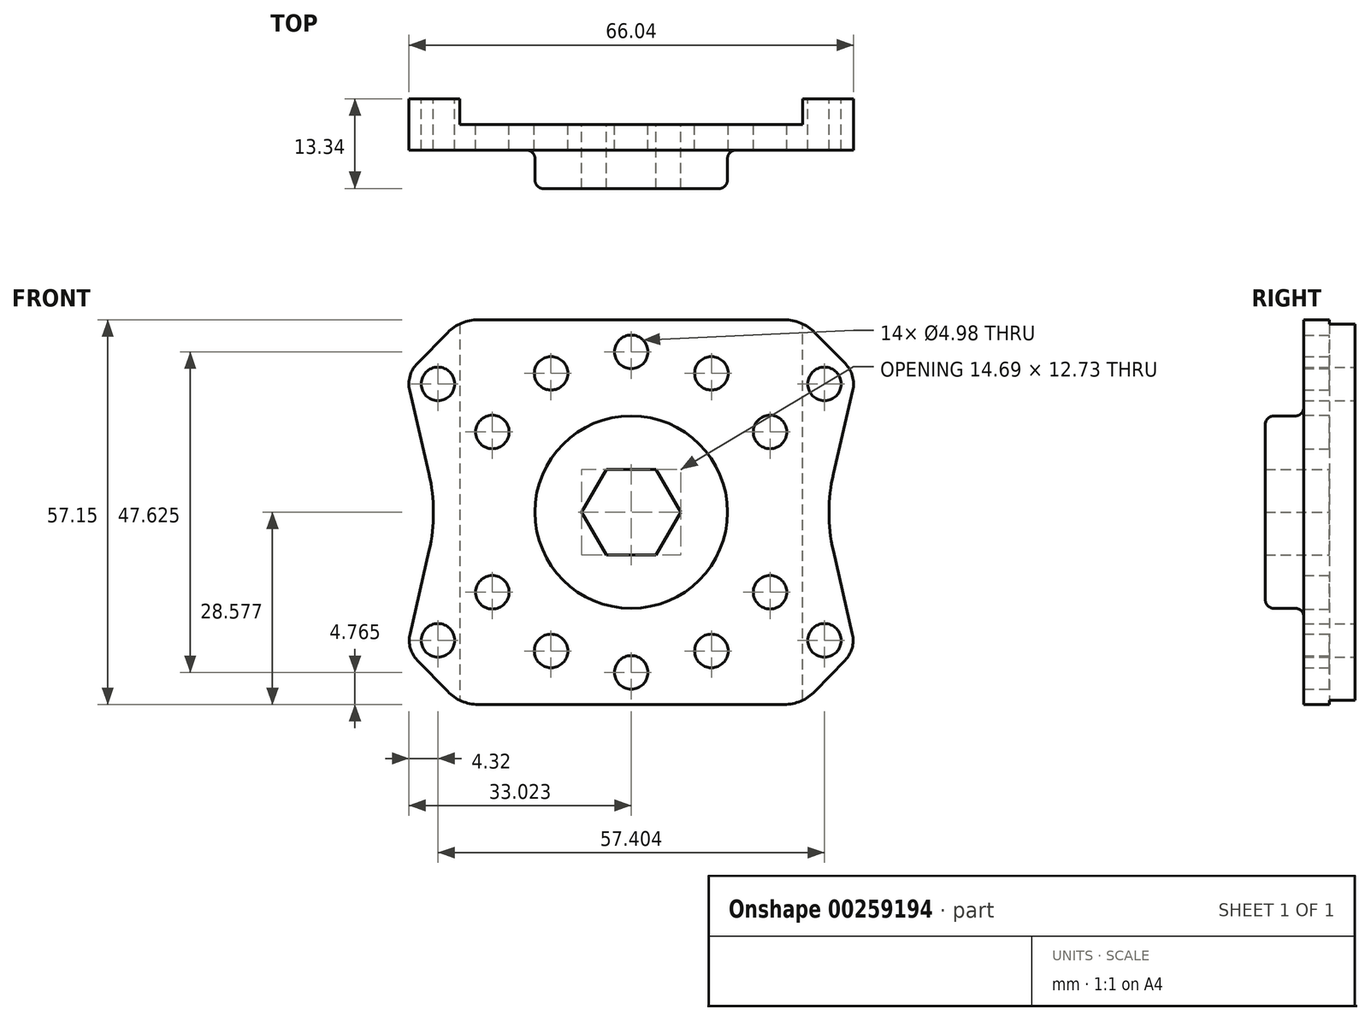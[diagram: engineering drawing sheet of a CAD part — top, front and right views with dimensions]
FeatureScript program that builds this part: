
annotation { "Feature Type Name" : "Feature", "Feature Type Description" : "" }
export const myFeature = defineFeature(function(context is Context, id is Id, definition is map)
    precondition{}
    {
        {
            var Q0;
            Q0=qCreatedBy(makeId("Front.planeOp"),FACE);
            var sketch = newSketch(context, id + "F0", { "sketchPlane" : qUnion([Q0])});
            skLineSegment(sketch, "E0.bottom", {"start": v(-23.4, 28.57) * mm, "end": v(22.07, 28.57) * mm});
            skLineSegment(sketch, "E0.top", {"start": v(-23.38, -28.58) * mm, "end": v(22.04, -28.58) * mm});
            skCircle(sketch, "E1", {"center": v(28.03, 19.05) * mm, "radius": 2.49 * mm});
            skCircle(sketch, "E2", {"center": v(28.03, -19.05) * mm, "radius": 2.49 * mm});
            skArc(sketch, "E3", {"start": v(32.24, 18.07) * mm, "mid": v(32.2, 20.21) * mm, "end": v(31.12, 22.07) * mm});
            skArc(sketch, "E4", {"start": v(31.1, -22.02) * mm, "mid": v(32.14, -20.2) * mm, "end": v(32.19, -18.1) * mm});
            skLineSegment(sketch, "E5", {"start": v(26.6, 26.67) * mm, "end": v(31.12, 22.07) * mm});
            skLineSegment(sketch, "E6", {"start": v(26.6, -26.65) * mm, "end": v(31.1, -22.02) * mm});
            skLineSegment(sketch, "E7", {"start": v(29.36, 5.71) * mm, "end": v(32.24, 18.07) * mm});
            skLineSegment(sketch, "E8", {"start": v(29.35, -5.72) * mm, "end": v(32.19, -18.1) * mm});
            skPoint(sketch, "E9.visualSharp", {"position": v(28.03, 0) * mm});
            skArc(sketch, "E9.filletArc", {"start": v(29.36, 5.71) * mm, "mid": v(28.7, 0) * mm, "end": v(29.35, -5.72) * mm});
            skLineSegment(sketch, "E10", {"start": v(-0.67, 28.57) * mm, "end": v(-0.67, -28.58) * mm, "construction": true});
            skLineSegment(sketch, "E11.MirrorCS", {"start": v(-27.93, 26.67) * mm, "end": v(-32.45, 22.07) * mm});
            skCircle(sketch, "E12.MirrorC", {"center": v(-29.37, 19.05) * mm, "radius": 2.49 * mm});
            skArc(sketch, "E13.MirrorCS", {"start": v(-33.58, 18.07) * mm, "mid": v(-33.53, 20.21) * mm, "end": v(-32.45, 22.07) * mm});
            skLineSegment(sketch, "E14.MirrorCS", {"start": v(-30.7, 5.71) * mm, "end": v(-33.58, 18.07) * mm});
            skArc(sketch, "E15.MirrorCS", {"start": v(-30.7, 5.71) * mm, "mid": v(-30.04, 0) * mm, "end": v(-30.68, -5.72) * mm});
            skLineSegment(sketch, "E16.MirrorCS", {"start": v(-30.68, -5.72) * mm, "end": v(-33.52, -18.1) * mm});
            skArc(sketch, "E17.MirrorCS", {"start": v(-32.43, -22.02) * mm, "mid": v(-33.47, -20.2) * mm, "end": v(-33.52, -18.1) * mm});
            skCircle(sketch, "E18.MirrorC", {"center": v(-29.37, -19.05) * mm, "radius": 2.49 * mm});
            skLineSegment(sketch, "E19.MirrorCS", {"start": v(-27.94, -26.65) * mm, "end": v(-32.43, -22.02) * mm});
            skPoint(sketch, "E20.visualSharp", {"position": v(24.73, 28.57) * mm});
            skArc(sketch, "E20.filletArc", {"start": v(26.6, 26.67) * mm, "mid": v(24.53, 28.08) * mm, "end": v(22.07, 28.57) * mm});
            skPoint(sketch, "E21.visualSharp", {"position": v(-26.07, 28.57) * mm});
            skArc(sketch, "E21.filletArc", {"start": v(-23.4, 28.57) * mm, "mid": v(-25.86, 28.08) * mm, "end": v(-27.93, 26.67) * mm});
            skPoint(sketch, "E22.visualSharp", {"position": v(-26.07, -28.58) * mm});
            skArc(sketch, "E22.filletArc", {"start": v(-27.94, -26.65) * mm, "mid": v(-25.85, -28.08) * mm, "end": v(-23.38, -28.58) * mm});
            skPoint(sketch, "E23.visualSharp", {"position": v(24.73, -28.58) * mm});
            skArc(sketch, "E23.filletArc", {"start": v(22.04, -28.58) * mm, "mid": v(24.52, -28.08) * mm, "end": v(26.6, -26.65) * mm});
            skCircle(sketch, "E24", {"center": v(-0.67, 23.8) * mm, "radius": 2.49 * mm});
            skCircle(sketch, "E25.1.0", {"center": v(-12.57, 20.62) * mm, "radius": 2.49 * mm});
            skCircle(sketch, "E25.2.0", {"center": v(-21.29, 11.9) * mm, "radius": 2.49 * mm});
            skCircle(sketch, "E25.4.0", {"center": v(-21.29, -11.9) * mm, "radius": 2.49 * mm});
            skCircle(sketch, "E25.5.0", {"center": v(-12.57, -20.62) * mm, "radius": 2.49 * mm});
            skPoint(sketch, "E25.center", {"position": v(-0.67, 0) * mm});
            skCircle(sketch, "E26.1.6.0", {"center": v(-0.67, -23.82) * mm, "radius": 2.49 * mm});
            skCircle(sketch, "E26.1.7.0", {"center": v(11.24, -20.62) * mm, "radius": 2.49 * mm});
            skCircle(sketch, "E26.1.8.0", {"center": v(19.95, -11.9) * mm, "radius": 2.49 * mm});
            skCircle(sketch, "E26.1.10.0", {"center": v(19.95, 11.9) * mm, "radius": 2.49 * mm});
            skCircle(sketch, "E26.1.11.0", {"center": v(11.24, 20.62) * mm, "radius": 2.49 * mm});
            skCircle(sketch, "E27.cCircle", {"center": v(-0.67, 0) * mm, "radius": 6.36 * mm, "construction": true});
            skLineSegment(sketch, "E27.0", {"start": v(-4.34, 6.36) * mm, "end": v(3, 6.36) * mm});
            skLineSegment(sketch, "E27.1", {"start": v(3, 6.36) * mm, "end": v(6.68, 0) * mm});
            skLineSegment(sketch, "E27.2", {"start": v(6.68, 0) * mm, "end": v(3, -6.37) * mm});
            skLineSegment(sketch, "E27.3", {"start": v(3, -6.37) * mm, "end": v(-4.34, -6.37) * mm});
            skLineSegment(sketch, "E27.4", {"start": v(-4.34, -6.37) * mm, "end": v(-8.01, 0) * mm});
            skLineSegment(sketch, "E27.5", {"start": v(-8.01, 0) * mm, "end": v(-4.34, 6.36) * mm});
            skPoint(sketch, "E27.0.midPoint", {"position": v(-0.67, 6.36) * mm});
            skLineSegment(sketch, "E28", {"start": v(-26.13, 27.96) * mm, "end": v(-26.13, -27.95) * mm});
            skLineSegment(sketch, "E29", {"start": v(24.8, -27.95) * mm, "end": v(24.8, 27.96) * mm});
            skCircle(sketch, "E30", {"center": v(-0.67, 0) * mm, "radius": 14.3 * mm});
            skCircle(sketch, "E31", {"center": v(-0.67, 0) * mm, "radius": 28.58 * mm, "construction": true});
            skSolve(sketch);
        }
        {
            var Q0;
            Q0=makeQuery(id+"F0.imprint","IMPRINT",FACE,{"disambiguationData":[TD([[makeQuery(id+"F0.imprint","IMPRINT",EDGE,{"derivedFrom":sQuery(id+"F0.wireOp",EDGE,"E0.bottom")}),-1.0]])]});
            var Q1;
            Q1=makeQuery(id+"F0.imprint","IMPRINT",FACE,{"disambiguationData":[TD([[makeQuery(id+"F0.imprint","IMPRINT",EDGE,{"derivedFrom":sQuery(id+"F0.wireOp",EDGE,"E27.0")}),1.0]])]});
            var Q2;
            Q2=makeQuery(id+"F0.imprint","IMPRINT",FACE,{"disambiguationData":[TD([[makeQuery(id+"F0.imprint","IMPRINT",EDGE,{"derivedFrom":sQuery(id+"F0.wireOp",EDGE,"E1")}),-1.0]])]});
            var Q3;
            {var subQ1=sQuery(id+"F0.wireOp",EDGE,"E11.MirrorCS");Q3=makeQuery(id+"F0.imprint","IMPRINT",FACE,{"disambiguationData":[TD([[makeQuery(id+"F0.imprint","IMPRINT",EDGE,{"derivedFrom":subQ1}),1.0]])]});}
            extrude(context, id + "F1", {"entities" : qUnion([Q0, Q1, Q2, Q3]), "depth" : 3.8 * mm});
        }
        {
            var Q0;
            Q0=makeQuery(id+"F0.imprint","IMPRINT",FACE,{"disambiguationData":[TD([[makeQuery(id+"F0.imprint","IMPRINT",EDGE,{"derivedFrom":sQuery(id+"F0.wireOp",EDGE,"E27.0")}),1.0]])]});
            extrude(context, id + "F2", {"entities" : qUnion([Q0]), "operationType" : NewBodyOperationType.ADD, "depth" : 9.52 * mm});
        }
        {
            var Q0;
            {var subQ1=sQuery(id+"F0.wireOp",EDGE,"E11.MirrorCS");Q0=makeQuery(id+"F0.imprint","IMPRINT",FACE,{"disambiguationData":[TD([[makeQuery(id+"F0.imprint","IMPRINT",EDGE,{"derivedFrom":subQ1}),1.0]])]});}
            var Q1;
            Q1=makeQuery(id+"F0.imprint","IMPRINT",FACE,{"disambiguationData":[TD([[makeQuery(id+"F0.imprint","IMPRINT",EDGE,{"derivedFrom":sQuery(id+"F0.wireOp",EDGE,"E1")}),-1.0]])]});
            extrude(context, id + "F3", {"entities" : qUnion([Q0, Q1]), "operationType" : NewBodyOperationType.ADD, "oppositeDirection" : true, "depth" : 3.8 * mm});
        }
        {
            var Q0;
            Q0=makeQuery(id+"F2.opExtrude","CAP_EDGE",EDGE,{"disambiguationData":[OSD([sQuery(id+"F0.wireOp",EDGE,"E30")])],"isStart":false});
            fillet(context, id + "F4", {"entities" : qUnion([Q0]), "radius" : 1.27 * mm, "tangentPropagation" : true, "allowEdgeOverflow" : false});
        }
        {
            var Q0;
            Q0=makeQuery(id+"F2.boolean.opBoolean","INTERSECT",EDGE,{"derivedFrom":[makeQuery(id+"F1.opExtrude","CAP_FACE",FACE,{"disambiguationData":[OSD([sQuery(id+"F0.wireOp",EDGE,"E0.bottom"),sQuery(id+"F0.wireOp",EDGE,"E0.top"),sQuery(id+"F0.wireOp",EDGE,"E1"),sQuery(id+"F0.wireOp",EDGE,"E2"),sQuery(id+"F0.wireOp",EDGE,"E3"),sQuery(id+"F0.wireOp",EDGE,"E4"),sQuery(id+"F0.wireOp",EDGE,"E5"),sQuery(id+"F0.wireOp",EDGE,"E6"),sQuery(id+"F0.wireOp",EDGE,"E7"),sQuery(id+"F0.wireOp",EDGE,"E8"),sQuery(id+"F0.wireOp",EDGE,"E9.filletArc"),sQuery(id+"F0.wireOp",EDGE,"E11.MirrorCS"),sQuery(id+"F0.wireOp",EDGE,"E12.MirrorC"),sQuery(id+"F0.wireOp",EDGE,"E13.MirrorCS"),sQuery(id+"F0.wireOp",EDGE,"E14.MirrorCS"),sQuery(id+"F0.wireOp",EDGE,"E15.MirrorCS"),sQuery(id+"F0.wireOp",EDGE,"E16.MirrorCS"),sQuery(id+"F0.wireOp",EDGE,"E17.MirrorCS"),sQuery(id+"F0.wireOp",EDGE,"E18.MirrorC"),sQuery(id+"F0.wireOp",EDGE,"E19.MirrorCS"),sQuery(id+"F0.wireOp",EDGE,"E20.filletArc"),sQuery(id+"F0.wireOp",EDGE,"E21.filletArc"),sQuery(id+"F0.wireOp",EDGE,"E22.filletArc"),sQuery(id+"F0.wireOp",EDGE,"E23.filletArc"),sQuery(id+"F0.wireOp",EDGE,"E24"),sQuery(id+"F0.wireOp",EDGE,"E25.1.0"),sQuery(id+"F0.wireOp",EDGE,"E25.2.0"),sQuery(id+"F0.wireOp",EDGE,"E25.4.0"),sQuery(id+"F0.wireOp",EDGE,"E25.5.0"),sQuery(id+"F0.wireOp",EDGE,"E26.1.6.0"),sQuery(id+"F0.wireOp",EDGE,"E26.1.7.0"),sQuery(id+"F0.wireOp",EDGE,"E26.1.8.0"),sQuery(id+"F0.wireOp",EDGE,"E26.1.10.0"),sQuery(id+"F0.wireOp",EDGE,"E26.1.11.0"),sQuery(id+"F0.wireOp",EDGE,"E27.0"),sQuery(id+"F0.wireOp",EDGE,"E27.1"),sQuery(id+"F0.wireOp",EDGE,"E27.2"),sQuery(id+"F0.wireOp",EDGE,"E27.3"),sQuery(id+"F0.wireOp",EDGE,"E27.4"),sQuery(id+"F0.wireOp",EDGE,"E27.5")])],"isStart":false}),makeQuery(id+"F2.opExtrude","SWEPT_FACE",FACE,{"disambiguationData":[OSD([sQuery(id+"F0.wireOp",EDGE,"E30")])]})]});
            fillet(context, id + "F5", {"entities" : qUnion([Q0]), "radius" : 1.27 * mm, "tangentPropagation" : true, "allowEdgeOverflow" : false});
        }
    });
